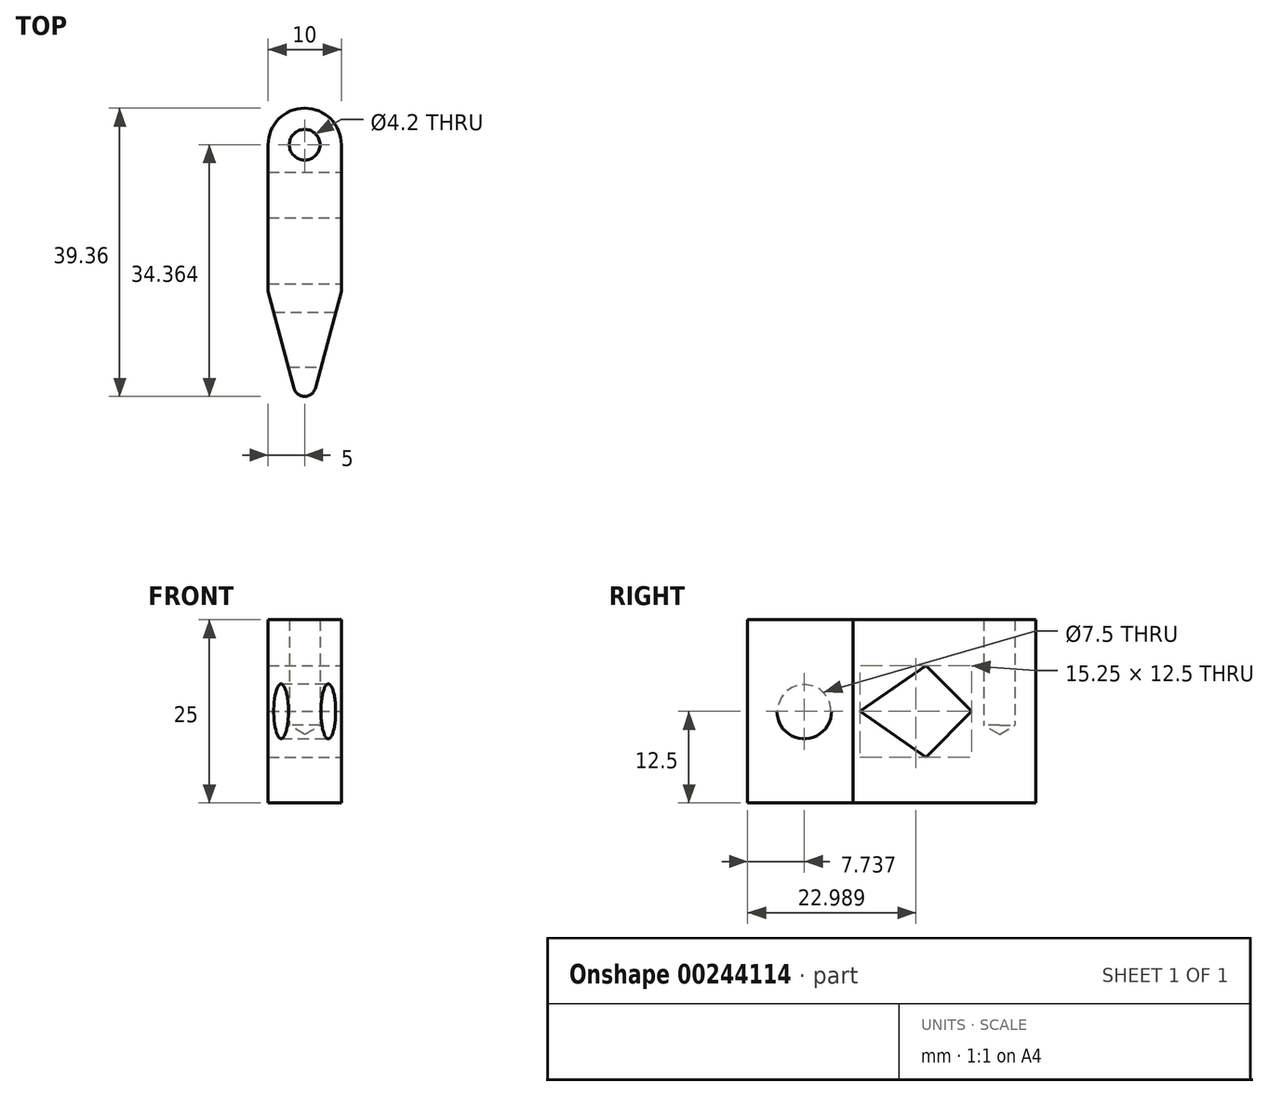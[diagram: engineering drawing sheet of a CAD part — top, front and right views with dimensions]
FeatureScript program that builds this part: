
annotation { "Feature Type Name" : "Feature", "Feature Type Description" : "" }
export const myFeature = defineFeature(function(context is Context, id is Id, definition is map)
    precondition{}
    {
        {
            var Q0;
            Q0=qCreatedBy(makeId("Top.planeOp"),FACE);
            var sketch = newSketch(context, id + "F0", { "sketchPlane" : qUnion([Q0])});
            skLineSegment(sketch, "E0.bottom", {"start": v(5, 16.41) * mm, "end": v(-5, 16.41) * mm});
            skLineSegment(sketch, "E0.top", {"start": v(5, -3.59) * mm, "end": v(-5, -3.59) * mm});
            skLineSegment(sketch, "E0.left", {"start": v(5, 16.41) * mm, "end": v(5, -3.59) * mm});
            skLineSegment(sketch, "E0.right", {"start": v(-5, 16.41) * mm, "end": v(-5, -3.59) * mm});
            skPoint(sketch, "E0.middle", {"position": v(0, 6.41) * mm});
            skArc(sketch, "E1", {"start": v(-5, 16.41) * mm, "mid": v(0, 21.41) * mm, "end": v(5, 16.41) * mm});
            skLineSegment(sketch, "E2", {"start": v(0, 6.41) * mm, "end": v(0, -50.9) * mm, "construction": true});
            skPoint(sketch, "E2.endSnap0", {"position": v(0, -3.59) * mm});
            skLineSegment(sketch, "E3", {"start": v(-5, -3.59) * mm, "end": v(-1.45, -16.84) * mm});
            skLineSegment(sketch, "E4", {"start": v(1.45, -16.84) * mm, "end": v(5, -3.59) * mm});
            skPoint(sketch, "E5.visualSharp", {"position": v(0, -22.25) * mm});
            skArc(sketch, "E5.filletArc", {"start": v(-1.45, -16.84) * mm, "mid": v(0, -17.95) * mm, "end": v(1.45, -16.84) * mm});
            skSolve(sketch);
        }
        {
            var Q0;
            Q0=makeQuery(id+"F0.imprint","IMPRINT",FACE,{"disambiguationData":[TD([[makeQuery(id+"F0.imprint","IMPRINT",EDGE,{"derivedFrom":sQuery(id+"F0.wireOp",EDGE,"E0.top")}),1.0]])]});
            var Q1;
            Q1=makeQuery(id+"F0.imprint","IMPRINT",FACE,{"disambiguationData":[TD([[makeQuery(id+"F0.imprint","IMPRINT",EDGE,{"derivedFrom":sQuery(id+"F0.wireOp",EDGE,"E0.bottom")}),1.0]])]});
            var Q2;
            Q2=makeQuery(id+"F0.imprint","IMPRINT",FACE,{"disambiguationData":[TD([[makeQuery(id+"F0.imprint","IMPRINT",EDGE,{"derivedFrom":sQuery(id+"F0.wireOp",EDGE,"E0.bottom")}),-1.0]])]});
            extrude(context, id + "F1", {"entities" : qUnion([Q0, Q1, Q2]), "depth" : 25 * mm});
        }
        {
            var Q0;
            Q0=makeQuery(id+"F1.opExtrude","SWEPT_FACE",FACE,{"disambiguationData":[OSD([sQuery(id+"F0.wireOp",EDGE,"E0.left")])]});
            var sketch = newSketch(context, id + "F2", { "sketchPlane" : qUnion([Q0])});
            skLineSegment(sketch, "E6", {"start": v(-3.59, 12.5) * mm, "end": v(16.41, 12.5) * mm, "construction": true});
            skLineSegment(sketch, "E7", {"start": v(6.41, 0) * mm, "end": v(6.41, 25) * mm, "construction": true});
            skLineSegment(sketch, "E8", {"start": v(6.41, 18.75) * mm, "end": v(-2.59, 12.5) * mm});
            skLineSegment(sketch, "E9", {"start": v(-2.59, 12.5) * mm, "end": v(6.41, 6.25) * mm});
            skLineSegment(sketch, "E10", {"start": v(6.41, 6.25) * mm, "end": v(12.66, 12.5) * mm});
            skLineSegment(sketch, "E11", {"start": v(12.66, 12.5) * mm, "end": v(6.41, 18.75) * mm});
            skSolve(sketch);
        }
        {
            var Q0;
            Q0=makeQuery(id+"F2.imprint","IMPRINT",FACE,{"disambiguationData":[TD([[makeQuery(id+"F2.imprint","IMPRINT",EDGE,{"derivedFrom":sQuery(id+"F2.wireOp",EDGE,"E8")}),1.0]])]});
            extrude(context, id + "F3", {"entities" : qUnion([Q0]), "operationType" : NewBodyOperationType.REMOVE, "endBound" : BoundingType.THROUGH_ALL, "oppositeDirection" : true, "depth" : 25 * mm});
        }
        {
            var Q0;
            Q0=qCreatedBy(makeId("Right.planeOp"),FACE);
            var sketch = newSketch(context, id + "F4", { "sketchPlane" : qUnion([Q0])});
            skLineSegment(sketch, "E12.0.0", {"start": v(-16.84, 0) * mm, "end": v(-3.59, 0) * mm, "construction": true});
            skLineSegment(sketch, "E12.0.1", {"start": v(-3.59, 0) * mm, "end": v(-3.59, 25) * mm, "construction": true});
            skLineSegment(sketch, "E12.0.2", {"start": v(-3.59, 25) * mm, "end": v(-16.84, 25) * mm, "construction": true});
            skLineSegment(sketch, "E12.0.3", {"start": v(-16.84, 25) * mm, "end": v(-16.84, 0) * mm, "construction": true});
            skLineSegment(sketch, "E13", {"start": v(-16.84, 0) * mm, "end": v(-3.59, 25) * mm, "construction": true});
            skPoint(sketch, "E14", {"position": v(-10.21, 12.5) * mm});
            skCircle(sketch, "E15", {"center": v(-10.21, 12.5) * mm, "radius": 3.75 * mm});
            skSolve(sketch);
        }
        {
            var Q0;
            Q0=qSketchRegion(id+"F4",true);
            extrude(context, id + "F5", {"entities" : qUnion([Q0]), "operationType" : NewBodyOperationType.REMOVE, "oppositeDirection" : true, "depth" : 25 * mm, "symmetric" : true});
        }
        {
            var Q0;
            Q0=makeQuery(id+"F1.opExtrude","CAP_FACE",FACE,{"disambiguationData":[OSD([sQuery(id+"F0.wireOp",EDGE,"E0.left"),sQuery(id+"F0.wireOp",EDGE,"E0.right"),sQuery(id+"F0.wireOp",EDGE,"E1"),sQuery(id+"F0.wireOp",EDGE,"E3"),sQuery(id+"F0.wireOp",EDGE,"E4")])],"isStart":false});
            var sketch = newSketch(context, id + "F6", { "sketchPlane" : qUnion([Q0])});
            skPoint(sketch, "E16", {"position": v(0, 16.41) * mm});
            skSolve(sketch);
        }
        {
            var Q0;
            Q0=sQuery(id+"F6.wireOp",VERTEX,"E16");
            var Q1;
            Q1=makeQuery(id+"F1.opExtrude","SWEPT_BODY",BODY,{"disambiguationData":[OSD([sQuery(id+"F0.wireOp",EDGE,"E0.left"),sQuery(id+"F0.wireOp",EDGE,"E0.right"),sQuery(id+"F0.wireOp",EDGE,"E1"),sQuery(id+"F0.wireOp",EDGE,"E3"),sQuery(id+"F0.wireOp",EDGE,"E4")])]});
            hole(context, id + "F7", {"style" : HoleStyle.SIMPLE, "endStyle" : HoleEndStyle.BLIND, "standardTappedOrClearance" : lookupTablePath({ "standard" : "ISO", "engagement" : "75%", "pitch" : "0.8 mm", "size" : "M5", "type" : "Tapped" }), "standardBlindInLast" : lookupTablePath({ "standard" : "ISO", "engagement" : "75%", "pitch" : "0.8 mm", "size" : "M5", "type" : "Tapped" }), "holeDiameter" : 4.2 * mm, "showTappedDepth" : true, "holeDepth" : 14.4 * mm, "tappedDepth" : 12 * mm, "tapClearance" : 3, "locations" : qUnion([Q0]), "scope" : qUnion([Q1]), "majorDiameter" : 5 * mm, "startStyle" : HoleStartStyle.PART});
        }
    });
